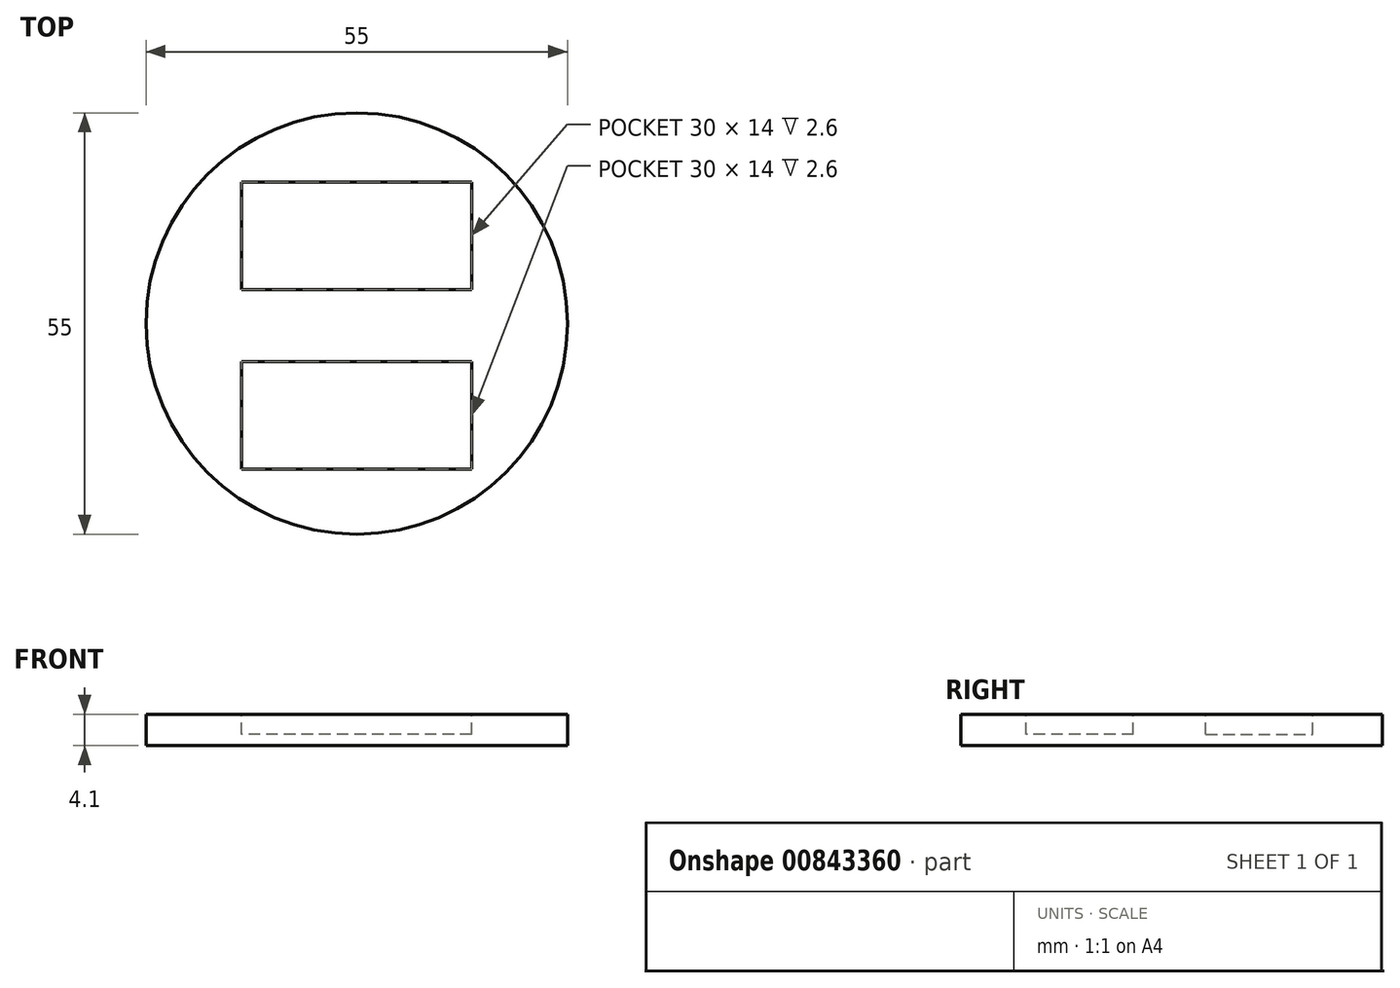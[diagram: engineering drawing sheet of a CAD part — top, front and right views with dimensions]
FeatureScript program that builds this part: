
annotation { "Feature Type Name" : "Feature", "Feature Type Description" : "" }
export const myFeature = defineFeature(function(context is Context, id is Id, definition is map)
    precondition{}
    {
        {
            var Q0;
            Q0=qCreatedBy(makeId("Top.planeOp"),FACE);
            var sketch = newSketch(context, id + "F0", { "sketchPlane" : qUnion([Q0])});
            skCircle(sketch, "E0", {"center": v(0, 0) * mm, "radius": 27.5 * mm});
            skSolve(sketch);
        }
        {
            var Q0;
            Q0 = qSketchRegion(id + "F0", true);
            extrude(context, id + "F1", {"entities" : qUnion([Q0]), "depth" : 4.1 * mm, "offsetDistance" : 25 * mm});
        }
        {
            var Q0;
            Q0=makeQuery(id+"F1.opExtrude","CAP_FACE",FACE,{"disambiguationData":[OSD([sQuery(id+"F0.wireOp",EDGE,"E0")])],"isStart":false});
            var sketch = newSketch(context, id + "F2", { "sketchPlane" : qUnion([Q0])});
            skLineSegment(sketch, "E1.bottom", {"start": v(15, 4.44) * mm, "end": v(-15, 4.44) * mm});
            skLineSegment(sketch, "E1.top", {"start": v(15, 18.44) * mm, "end": v(-15, 18.44) * mm});
            skLineSegment(sketch, "E1.left", {"start": v(15, 4.44) * mm, "end": v(15, 18.44) * mm});
            skLineSegment(sketch, "E1.right", {"start": v(-15, 4.44) * mm, "end": v(-15, 18.44) * mm});
            skPoint(sketch, "E1.middle", {"position": v(0, 11.44) * mm});
            skSolve(sketch);
        }
        {
            var Q0;
            Q0 = qSketchRegion(id + "F2", true);
            extrude(context, id + "F3", {"entities" : qUnion([Q0]), "operationType" : NewBodyOperationType.REMOVE, "oppositeDirection" : true, "depth" : 2.6 * mm, "offsetDistance" : 25 * mm});
        }
        {
            var Q0;
            Q0=makeQuery(id+"F1.opExtrude","CAP_FACE",FACE,{"disambiguationData":[OSD([sQuery(id+"F0.wireOp",EDGE,"E0")])],"isStart":false});
            var sketch = newSketch(context, id + "F4", { "sketchPlane" : qUnion([Q0])});
            skLineSegment(sketch, "E2.bottom", {"start": v(-15, -5) * mm, "end": v(15, -5) * mm});
            skLineSegment(sketch, "E2.top", {"start": v(-15, -19) * mm, "end": v(15, -19) * mm});
            skLineSegment(sketch, "E2.left", {"start": v(-15, -5) * mm, "end": v(-15, -19) * mm});
            skLineSegment(sketch, "E2.right", {"start": v(15, -5) * mm, "end": v(15, -19) * mm});
            skPoint(sketch, "E2.middle", {"position": v(0, -12) * mm});
            skSolve(sketch);
        }
        {
            var Q0;
            Q0=makeQuery(id+"F4.imprint","IMPRINT",FACE,{"disambiguationData":[TD([[makeQuery(id+"F4.imprint","IMPRINT",EDGE,{"derivedFrom":sQuery(id+"F4.wireOp",EDGE,"E2.bottom")}),-1.0]])]});
            extrude(context, id + "F5", {"entities" : qUnion([Q0]), "operationType" : NewBodyOperationType.REMOVE, "oppositeDirection" : true, "depth" : 2.6 * mm, "offsetDistance" : 25 * mm});
        }
    });
